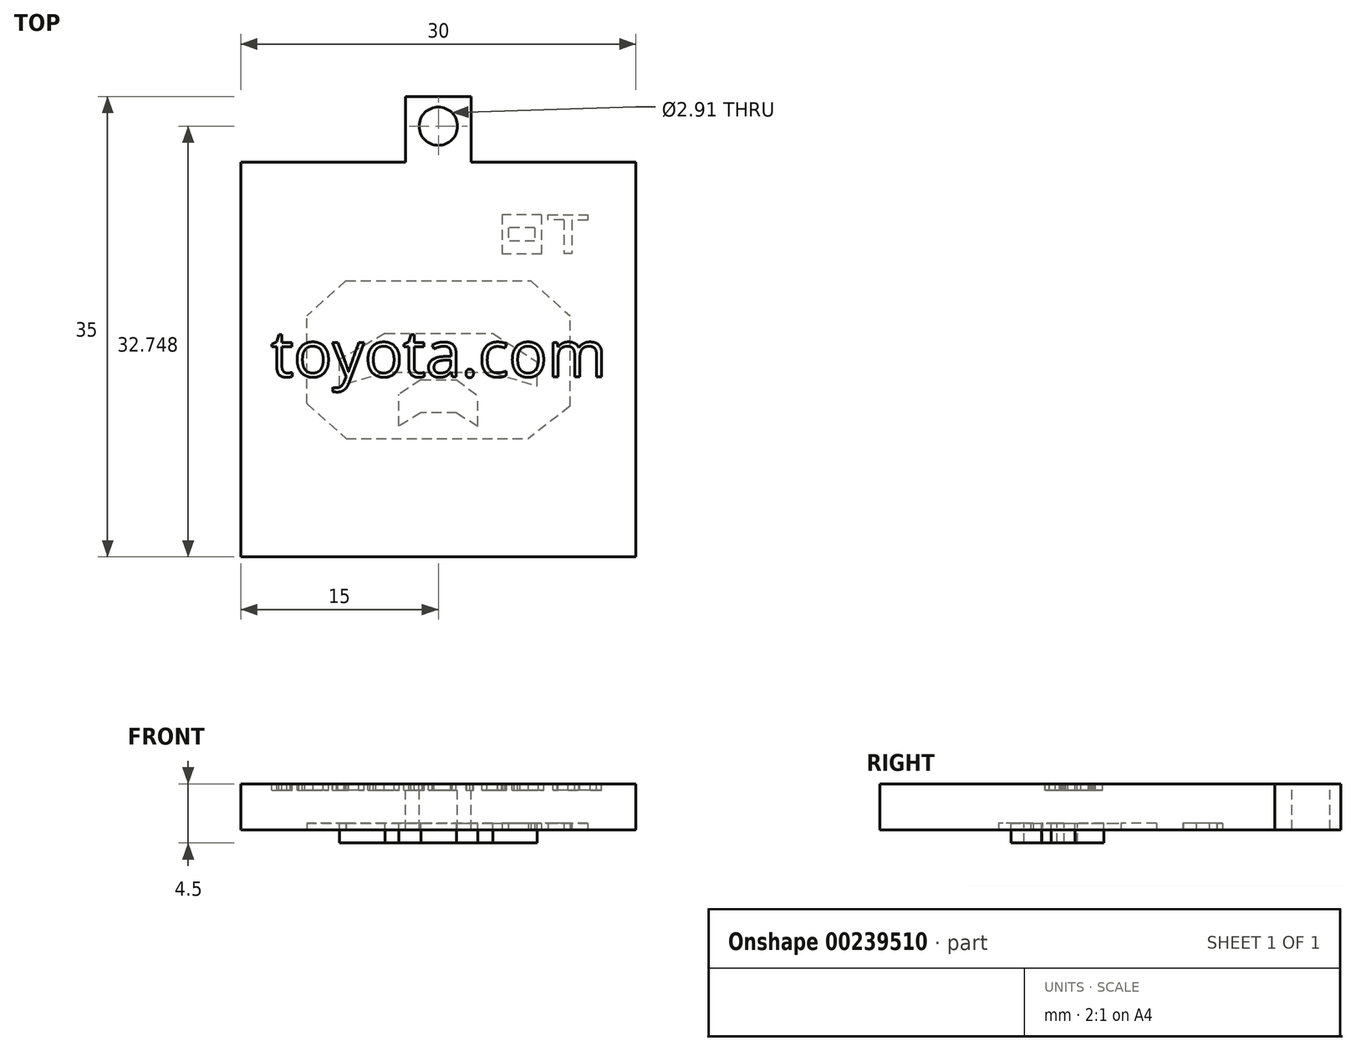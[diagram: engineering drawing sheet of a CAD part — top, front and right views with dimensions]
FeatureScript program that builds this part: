
annotation { "Feature Type Name" : "Feature", "Feature Type Description" : "" }
export const myFeature = defineFeature(function(context is Context, id is Id, definition is map)
    precondition{}
    {
        {
            var Q0;
            Q0=qCreatedBy(makeId("Top.planeOp"),FACE);
            var sketch = newSketch(context, id + "F0", { "sketchPlane" : qUnion([Q0])});
            skLineSegment(sketch, "E0.bottom", {"start": v(15, -15) * mm, "end": v(-15, -15) * mm});
            skLineSegment(sketch, "E0.top", {"start": v(15, 15) * mm, "end": v(-15, 15) * mm});
            skLineSegment(sketch, "E0.left", {"start": v(15, -15) * mm, "end": v(15, 15) * mm});
            skLineSegment(sketch, "E0.right", {"start": v(-15, -15) * mm, "end": v(-15, 15) * mm});
            skPoint(sketch, "E0.middle", {"position": v(0, 0) * mm});
            skSolve(sketch);
        }
        {
            var Q0;
            Q0=makeQuery(id+"F0.imprint","IMPRINT",FACE,{"disambiguationData":[TD([[makeQuery(id+"F0.imprint","IMPRINT",EDGE,{"derivedFrom":sQuery(id+"F0.wireOp",EDGE,"E0.bottom")}),-1.0]])]});
            extrude(context, id + "F1", {"entities" : qUnion([Q0]), "endBound" : BoundingType.SYMMETRIC, "depth" : 3.5 * mm});
        }
        {
            var Q0;
            Q0=makeQuery(id+"F1.opExtrude","CAP_FACE",FACE,{"disambiguationData":[OSD([sQuery(id+"F0.wireOp",EDGE,"E0.bottom"),sQuery(id+"F0.wireOp",EDGE,"E0.top"),sQuery(id+"F0.wireOp",EDGE,"E0.left"),sQuery(id+"F0.wireOp",EDGE,"E0.right")])],"isStart":false});
            var sketch = newSketch(context, id + "F2", { "sketchPlane" : qUnion([Q0])});
            skLineSegment(sketch, "E1.bottom", {"start": v(-2.5, 15) * mm, "end": v(2.5, 15) * mm});
            skLineSegment(sketch, "E1.top", {"start": v(-2.5, 20) * mm, "end": v(2.5, 20) * mm});
            skLineSegment(sketch, "E1.left", {"start": v(-2.5, 15) * mm, "end": v(-2.5, 20) * mm});
            skLineSegment(sketch, "E1.right", {"start": v(2.5, 15) * mm, "end": v(2.5, 20) * mm});
            skSolve(sketch);
        }
        {
            var Q0;
            Q0=makeQuery(id+"F2.imprint","IMPRINT",FACE,{"disambiguationData":[TD([[makeQuery(id+"F2.imprint","IMPRINT",EDGE,{"derivedFrom":sQuery(id+"F2.wireOp",EDGE,"E1.bottom")}),-1.0]])]});
            extrude(context, id + "F3", {"entities" : qUnion([Q0]), "operationType" : NewBodyOperationType.ADD, "oppositeDirection" : true, "depth" : 3.5 * mm});
        }
        {
            var Q0;
            Q0=makeQuery(id+"F3.boolean.opBoolean","MERGE",FACE,{"derivedFrom":[makeQuery(id+"F1.opExtrude","CAP_FACE",FACE,{"disambiguationData":[OSD([sQuery(id+"F0.wireOp",EDGE,"E0.bottom"),sQuery(id+"F0.wireOp",EDGE,"E0.top"),sQuery(id+"F0.wireOp",EDGE,"E0.left"),sQuery(id+"F0.wireOp",EDGE,"E0.right")])],"isStart":false}),makeQuery(id+"F3.opExtrude","CAP_FACE",FACE,{"disambiguationData":[OSD([sQuery(id+"F2.wireOp",EDGE,"E1.bottom"),sQuery(id+"F2.wireOp",EDGE,"E1.top"),sQuery(id+"F2.wireOp",EDGE,"E1.left"),sQuery(id+"F2.wireOp",EDGE,"E1.right")])],"isStart":true})]});
            var sketch = newSketch(context, id + "F4", { "sketchPlane" : qUnion([Q0])});
            skCircle(sketch, "E2", {"center": v(0, 17.75) * mm, "radius": 1.46 * mm});
            skSolve(sketch);
        }
        {
            var Q0;
            Q0 = qSketchRegion(id + "F4", true);
            extrude(context, id + "F5", {"entities" : qUnion([Q0]), "operationType" : NewBodyOperationType.REMOVE, "endBound" : BoundingType.THROUGH_ALL, "oppositeDirection" : true, "depth" : 25 * mm});
        }
        {
            var Q0;
            Q0=makeQuery(id+"F3.boolean.opBoolean","MERGE",FACE,{"derivedFrom":[makeQuery(id+"F1.opExtrude","CAP_FACE",FACE,{"disambiguationData":[OSD([sQuery(id+"F0.wireOp",EDGE,"E0.bottom"),sQuery(id+"F0.wireOp",EDGE,"E0.top"),sQuery(id+"F0.wireOp",EDGE,"E0.left"),sQuery(id+"F0.wireOp",EDGE,"E0.right")])],"isStart":true}),makeQuery(id+"F3.opExtrude","CAP_FACE",FACE,{"disambiguationData":[OSD([sQuery(id+"F2.wireOp",EDGE,"E1.bottom"),sQuery(id+"F2.wireOp",EDGE,"E1.top"),sQuery(id+"F2.wireOp",EDGE,"E1.left"),sQuery(id+"F2.wireOp",EDGE,"E1.right")])],"isStart":false})]});
            var sketch = newSketch(context, id + "F6", { "sketchPlane" : qUnion([Q0])});
            skLineSegment(sketch, "E3.bottom", {"start": v(-7, 6) * mm, "end": v(6.85, 6) * mm});
            skLineSegment(sketch, "E3.top", {"start": v(-7.03, -6) * mm, "end": v(7.03, -6) * mm});
            skLineSegment(sketch, "E3.left", {"start": v(-10, 3.35) * mm, "end": v(-10, -3.32) * mm});
            skLineSegment(sketch, "E3.right", {"start": v(10, 3.53) * mm, "end": v(10, -3.33) * mm});
            skPoint(sketch, "E3.middle", {"position": v(0, 0) * mm});
            skLineSegment(sketch, "E4", {"start": v(-7.03, -6) * mm, "end": v(-10, -3.32) * mm});
            skLineSegment(sketch, "E5", {"start": v(7.03, -6) * mm, "end": v(10, -3.33) * mm});
            skLineSegment(sketch, "E6", {"start": v(10, 3.53) * mm, "end": v(6.85, 6) * mm});
            skLineSegment(sketch, "E7", {"start": v(-10, 3.35) * mm, "end": v(-7, 6) * mm});
            skPoint(sketch, "E8.orphan", {"position": v(10, -6) * mm});
            skPoint(sketch, "E9.orphan", {"position": v(-10, -6) * mm});
            skPoint(sketch, "E10.orphan", {"position": v(10, 6) * mm});
            skPoint(sketch, "E11.orphan", {"position": v(-10, 6) * mm});
            skSolve(sketch);
        }
        {
            var Q0;
            Q0 = qSketchRegion(id + "F6", true);
            extrude(context, id + "F7", {"entities" : qUnion([Q0]), "operationType" : NewBodyOperationType.REMOVE, "oppositeDirection" : true, "depth" : 0.5 * mm});
        }
        {
            var Q0;
            Q0=makeQuery(id+"F7.boolean.opBoolean","COPY",FACE,{"derivedFrom":makeQuery(id+"F7.opExtrude","CAP_FACE",FACE,{"disambiguationData":[OSD([sQuery(id+"F6.wireOp",EDGE,"E3.bottom"),sQuery(id+"F6.wireOp",EDGE,"E3.top"),sQuery(id+"F6.wireOp",EDGE,"E3.left"),sQuery(id+"F6.wireOp",EDGE,"E3.right"),sQuery(id+"F6.wireOp",EDGE,"E4"),sQuery(id+"F6.wireOp",EDGE,"E5"),sQuery(id+"F6.wireOp",EDGE,"E6"),sQuery(id+"F6.wireOp",EDGE,"E7")])],"isStart":false})});
            var sketch = newSketch(context, id + "F8", { "sketchPlane" : qUnion([Q0])});
            skLineSegment(sketch, "E12.top", {"start": v(-4.04, -2) * mm, "end": v(4.14, -2) * mm});
            skLineSegment(sketch, "E12.left", {"start": v(-7.5, 2) * mm, "end": v(-7.5, 0) * mm});
            skLineSegment(sketch, "E12.right", {"start": v(7.5, 2) * mm, "end": v(7.5, 0.17) * mm});
            skPoint(sketch, "E12.middle", {"position": v(0, 0) * mm});
            skLineSegment(sketch, "E13", {"start": v(4.14, -2) * mm, "end": v(7.5, 0.17) * mm});
            skLineSegment(sketch, "E14", {"start": v(-4.04, -2) * mm, "end": v(-7.5, 0) * mm});
            skPoint(sketch, "E15.orphan", {"position": v(7.5, -2) * mm});
            skPoint(sketch, "E16.orphan", {"position": v(-7.5, -2) * mm});
            skLineSegment(sketch, "E17", {"start": v(4.14, 1) * mm, "end": v(7.5, 2) * mm});
            skLineSegment(sketch, "E18", {"start": v(4.14, 1) * mm, "end": v(-4.04, 1) * mm});
            skLineSegment(sketch, "E19", {"start": v(-4.04, 1) * mm, "end": v(-7.5, 2) * mm});
            skSolve(sketch);
        }
        {
            var Q0;
            Q0 = qSketchRegion(id + "F8", true);
            extrude(context, id + "F9", {"entities" : qUnion([Q0]), "operationType" : NewBodyOperationType.ADD, "depth" : 1.5 * mm});
        }
        {
            var Q0;
            Q0=makeQuery(id+"F7.boolean.opBoolean","COPY",FACE,{"derivedFrom":makeQuery(id+"F7.opExtrude","CAP_FACE",FACE,{"disambiguationData":[OSD([sQuery(id+"F6.wireOp",EDGE,"E3.bottom"),sQuery(id+"F6.wireOp",EDGE,"E3.top"),sQuery(id+"F6.wireOp",EDGE,"E3.left"),sQuery(id+"F6.wireOp",EDGE,"E3.right"),sQuery(id+"F6.wireOp",EDGE,"E4"),sQuery(id+"F6.wireOp",EDGE,"E5"),sQuery(id+"F6.wireOp",EDGE,"E6"),sQuery(id+"F6.wireOp",EDGE,"E7")])],"isStart":false})});
            var sketch = newSketch(context, id + "F10", { "sketchPlane" : qUnion([Q0])});
            skLineSegment(sketch, "E20.top", {"start": v(-1.32, 1.54) * mm, "end": v(1.38, 1.54) * mm});
            skLineSegment(sketch, "E20.left", {"start": v(-3, 5.04) * mm, "end": v(-3, 2.63) * mm});
            skLineSegment(sketch, "E20.right", {"start": v(3, 5.04) * mm, "end": v(3, 2.72) * mm});
            skPoint(sketch, "E20.middle", {"position": v(0, 3.3) * mm});
            skLineSegment(sketch, "E21", {"start": v(1.38, 1.54) * mm, "end": v(3, 2.72) * mm});
            skLineSegment(sketch, "E22", {"start": v(-1.32, 1.54) * mm, "end": v(-3, 2.63) * mm});
            skPoint(sketch, "E23.orphan", {"position": v(3, 1.54) * mm});
            skPoint(sketch, "E24.orphan", {"position": v(-3, 1.54) * mm});
            skLineSegment(sketch, "E25", {"start": v(1.38, 4.04) * mm, "end": v(-1.32, 4.04) * mm});
            skLineSegment(sketch, "E26", {"start": v(1.38, 4.04) * mm, "end": v(3, 5.04) * mm});
            skLineSegment(sketch, "E27", {"start": v(-1.32, 4.04) * mm, "end": v(-3, 5.04) * mm});
            skSolve(sketch);
        }
        {
            var Q0;
            Q0 = qSketchRegion(id + "F10", true);
            extrude(context, id + "F11", {"entities" : qUnion([Q0]), "operationType" : NewBodyOperationType.ADD, "depth" : 1.5 * mm});
        }
        {
            var Q0;
            Q0=makeQuery(id+"F3.boolean.opBoolean","MERGE",FACE,{"derivedFrom":[makeQuery(id+"F1.opExtrude","CAP_FACE",FACE,{"disambiguationData":[OSD([sQuery(id+"F0.wireOp",EDGE,"E0.bottom"),sQuery(id+"F0.wireOp",EDGE,"E0.top"),sQuery(id+"F0.wireOp",EDGE,"E0.left"),sQuery(id+"F0.wireOp",EDGE,"E0.right")])],"isStart":false}),makeQuery(id+"F3.opExtrude","CAP_FACE",FACE,{"disambiguationData":[OSD([sQuery(id+"F2.wireOp",EDGE,"E1.bottom"),sQuery(id+"F2.wireOp",EDGE,"E1.top"),sQuery(id+"F2.wireOp",EDGE,"E1.left"),sQuery(id+"F2.wireOp",EDGE,"E1.right")])],"isStart":true})]});
            var sketch = newSketch(context, id + "F12", { "sketchPlane" : qUnion([Q0])});
            skText(sketch, "E28", { "text": "toyota.com\n", "fontName": "OpenSans-Regular.ttf"});
            const initialGuessF12  = {"E28": [-0.01272, -0.0013, 1, 0, 0.0035]};
            skSetInitialGuess(sketch, initialGuessF12);
            skSolve(sketch);
        }
        {
            var Q0;
            Q0 = qSketchRegion(id + "F12", true);
            extrude(context, id + "F13", {"entities" : qUnion([Q0]), "operationType" : NewBodyOperationType.REMOVE, "oppositeDirection" : true, "depth" : 0.5 * mm});
        }
        {
            var Q0;
            Q0=makeQuery(id+"F3.boolean.opBoolean","MERGE",FACE,{"derivedFrom":[makeQuery(id+"F1.opExtrude","CAP_FACE",FACE,{"disambiguationData":[OSD([sQuery(id+"F0.wireOp",EDGE,"E0.bottom"),sQuery(id+"F0.wireOp",EDGE,"E0.top"),sQuery(id+"F0.wireOp",EDGE,"E0.left"),sQuery(id+"F0.wireOp",EDGE,"E0.right")])],"isStart":true}),makeQuery(id+"F3.opExtrude","CAP_FACE",FACE,{"disambiguationData":[OSD([sQuery(id+"F2.wireOp",EDGE,"E1.bottom"),sQuery(id+"F2.wireOp",EDGE,"E1.top"),sQuery(id+"F2.wireOp",EDGE,"E1.left"),sQuery(id+"F2.wireOp",EDGE,"E1.right")])],"isStart":false})]});
            var sketch = newSketch(context, id + "F14", { "sketchPlane" : qUnion([Q0])});
            skLineSegment(sketch, "E29", {"start": v(10.15, -10.6) * mm, "end": v(10.15, -8.05) * mm});
            skLineSegment(sketch, "E30", {"start": v(9.53, -10.63) * mm, "end": v(9.53, -8.05) * mm});
            skLineSegment(sketch, "E31", {"start": v(10.15, -8.05) * mm, "end": v(9.53, -8.05) * mm});
            skLineSegment(sketch, "E32", {"start": v(9.53, -10.63) * mm, "end": v(8.34, -10.63) * mm});
            skLineSegment(sketch, "E33", {"start": v(8.34, -10.63) * mm, "end": v(8.34, -11.02) * mm});
            skLineSegment(sketch, "E34", {"start": v(8.34, -11.02) * mm, "end": v(11.34, -11.02) * mm});
            skLineSegment(sketch, "E35", {"start": v(11.34, -11.02) * mm, "end": v(11.34, -10.6) * mm});
            skLineSegment(sketch, "E36", {"start": v(11.34, -10.6) * mm, "end": v(10.15, -10.6) * mm});
            skSolve(sketch);
        }
        {
            var Q0;
            Q0 = qSketchRegion(id + "F14", true);
            extrude(context, id + "F15", {"entities" : qUnion([Q0]), "operationType" : NewBodyOperationType.REMOVE, "oppositeDirection" : true, "depth" : 0.5 * mm});
        }
        {
            var Q0;
            Q0=makeQuery(id+"F3.boolean.opBoolean","MERGE",FACE,{"derivedFrom":[makeQuery(id+"F1.opExtrude","CAP_FACE",FACE,{"disambiguationData":[OSD([sQuery(id+"F0.wireOp",EDGE,"E0.bottom"),sQuery(id+"F0.wireOp",EDGE,"E0.top"),sQuery(id+"F0.wireOp",EDGE,"E0.left"),sQuery(id+"F0.wireOp",EDGE,"E0.right")])],"isStart":true}),makeQuery(id+"F3.opExtrude","CAP_FACE",FACE,{"disambiguationData":[OSD([sQuery(id+"F2.wireOp",EDGE,"E1.bottom"),sQuery(id+"F2.wireOp",EDGE,"E1.top"),sQuery(id+"F2.wireOp",EDGE,"E1.left"),sQuery(id+"F2.wireOp",EDGE,"E1.right")])],"isStart":false})]});
            var sketch = newSketch(context, id + "F16", { "sketchPlane" : qUnion([Q0])});
            skLineSegment(sketch, "E37.bottom", {"start": v(7.84, -11.02) * mm, "end": v(4.84, -11.02) * mm});
            skLineSegment(sketch, "E37.top", {"start": v(7.84, -8.02) * mm, "end": v(4.84, -8.02) * mm});
            skLineSegment(sketch, "E37.left", {"start": v(7.84, -11.02) * mm, "end": v(7.84, -8.02) * mm});
            skLineSegment(sketch, "E37.right", {"start": v(4.84, -11.02) * mm, "end": v(4.84, -8.02) * mm});
            skLineSegment(sketch, "E38.bottom", {"start": v(7.32, -10.02) * mm, "end": v(5.32, -10.02) * mm});
            skLineSegment(sketch, "E38.top", {"start": v(7.32, -9.02) * mm, "end": v(5.32, -9.02) * mm});
            skLineSegment(sketch, "E38.left", {"start": v(7.32, -10.02) * mm, "end": v(7.32, -9.02) * mm});
            skLineSegment(sketch, "E38.right", {"start": v(5.32, -10.02) * mm, "end": v(5.32, -9.02) * mm});
            skSolve(sketch);
        }
        {
            var Q0;
            Q0 = qSketchRegion(id + "F16", true);
            extrude(context, id + "F17", {"entities" : qUnion([Q0]), "operationType" : NewBodyOperationType.REMOVE, "oppositeDirection" : true, "depth" : 0.5 * mm});
        }
    });
